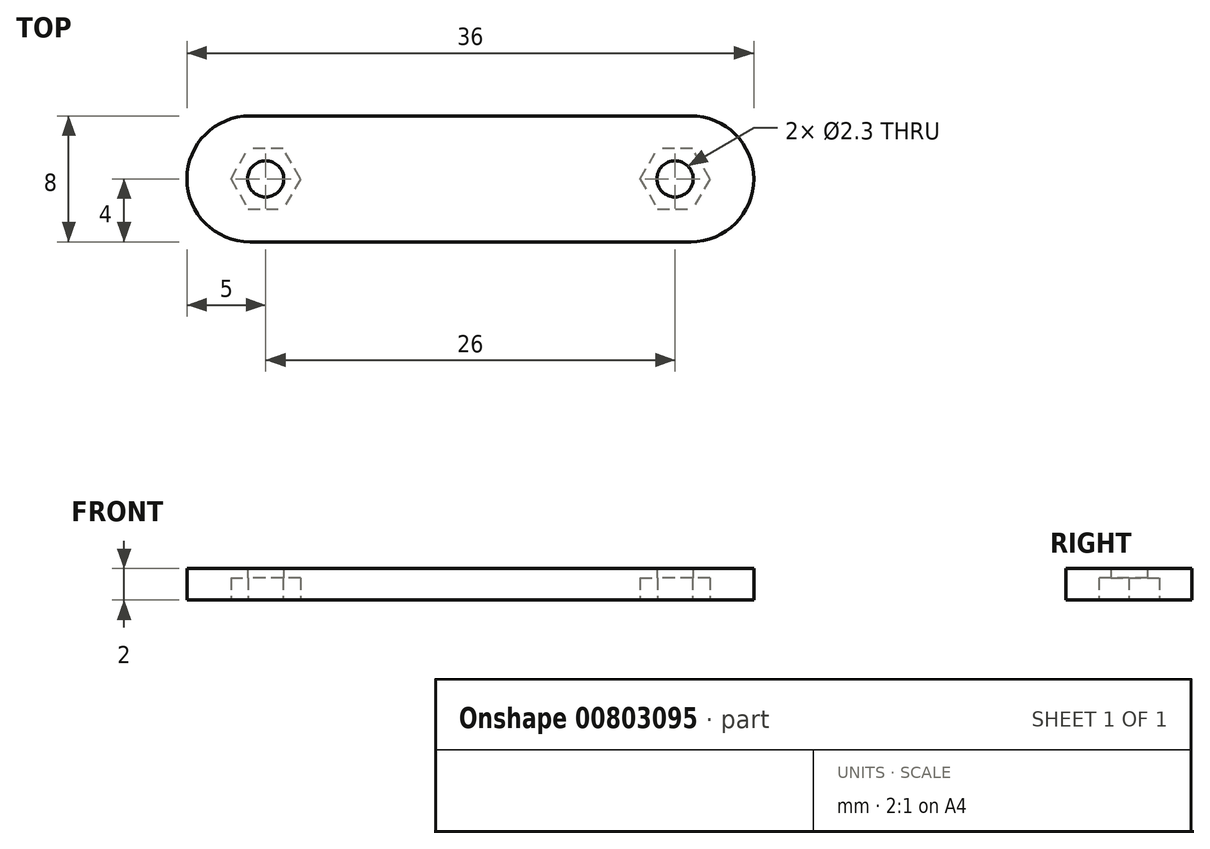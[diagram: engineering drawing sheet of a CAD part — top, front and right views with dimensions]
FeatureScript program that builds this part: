
annotation { "Feature Type Name" : "Feature", "Feature Type Description" : "" }
export const myFeature = defineFeature(function(context is Context, id is Id, definition is map)
    precondition{}
    {
        {
            var Q0;
            Q0=qCreatedBy(makeId("Top.planeOp"),FACE);
            var sketch = newSketch(context, id + "F0", { "sketchPlane" : qUnion([Q0])});
            skCircle(sketch, "E0", {"center": v(-13, 0) * mm, "radius": 1.15 * mm});
            skCircle(sketch, "E1.MirrorC", {"center": v(13, 0) * mm, "radius": 1.15 * mm});
            skSolve(sketch);
        }
        {
            var Q0;
            Q0=qCreatedBy(makeId("Top.planeOp"),FACE);
            var sketch = newSketch(context, id + "F1", { "sketchPlane" : qUnion([Q0])});
            skLineSegment(sketch, "E2.bottom", {"start": v(18, 4) * mm, "end": v(-18, 4) * mm});
            skLineSegment(sketch, "E2.top", {"start": v(18, -4) * mm, "end": v(-18, -4) * mm});
            skLineSegment(sketch, "E2.left", {"start": v(18, 4) * mm, "end": v(18, -4) * mm});
            skLineSegment(sketch, "E2.right", {"start": v(-18, 4) * mm, "end": v(-18, -4) * mm});
            skPoint(sketch, "E2.middle", {"position": v(0, 0) * mm});
            skSolve(sketch);
        }
        {
            var Q0;
            Q0=qCreatedBy(makeId("Top.planeOp"),FACE);
            var sketch = newSketch(context, id + "F2", { "sketchPlane" : qUnion([Q0])});
            skLineSegment(sketch, "E3", {"start": v(-13, 0) * mm, "end": v(-13, 4.8) * mm, "construction": true});
            skLineSegment(sketch, "E4", {"start": v(-13, 0) * mm, "end": v(-5.64, 0) * mm, "construction": true});
            skLineSegment(sketch, "E5", {"start": v(-13, 0) * mm, "end": v(-15.53, 4.38) * mm, "construction": true});
            skLineSegment(sketch, "E6", {"start": v(-10.79, 0) * mm, "end": v(-11.9, 1.91) * mm});
            skLineSegment(sketch, "E7", {"start": v(-11.9, 1.91) * mm, "end": v(-13, 1.91) * mm});
            skLineSegment(sketch, "E8.MirrorCS", {"start": v(-14.1, 1.91) * mm, "end": v(-13, 1.91) * mm});
            skLineSegment(sketch, "E9.MirrorCS", {"start": v(-15.21, 0) * mm, "end": v(-14.1, 1.91) * mm});
            skLineSegment(sketch, "E10.MirrorCS", {"start": v(-10.79, 0) * mm, "end": v(-11.9, -1.91) * mm});
            skLineSegment(sketch, "E11.MirrorCS", {"start": v(-11.9, -1.91) * mm, "end": v(-13, -1.91) * mm});
            skLineSegment(sketch, "E12.MirrorCS", {"start": v(-14.1, -1.91) * mm, "end": v(-13, -1.91) * mm});
            skLineSegment(sketch, "E13.MirrorCS", {"start": v(-15.21, 0) * mm, "end": v(-14.1, -1.91) * mm});
            skLineSegment(sketch, "E14.MirrorCS", {"start": v(15.21, 0) * mm, "end": v(14.1, -1.91) * mm});
            skLineSegment(sketch, "E15.MirrorCS", {"start": v(14.1, -1.91) * mm, "end": v(13, -1.91) * mm});
            skLineSegment(sketch, "E16.MirrorCS", {"start": v(14.1, 1.91) * mm, "end": v(13, 1.91) * mm});
            skLineSegment(sketch, "E17.MirrorCS", {"start": v(10.79, 0) * mm, "end": v(11.9, 1.91) * mm});
            skLineSegment(sketch, "E18.MirrorCS", {"start": v(15.21, 0) * mm, "end": v(14.1, 1.91) * mm});
            skLineSegment(sketch, "E19.MirrorCS", {"start": v(11.9, 1.91) * mm, "end": v(13, 1.91) * mm});
            skLineSegment(sketch, "E20.MirrorCS", {"start": v(11.9, -1.91) * mm, "end": v(13, -1.91) * mm});
            skLineSegment(sketch, "E21.MirrorCS", {"start": v(10.79, 0) * mm, "end": v(11.9, -1.91) * mm});
            skSolve(sketch);
        }
        {
            var Q0;
            Q0=qSketchRegion(id+"F1",true);
            extrude(context, id + "F3", {"entities" : qUnion([Q0]), "depth" : 2 * mm, "offsetDistance" : 25 * mm});
        }
        {
            var Q0;
            Q0=qSketchRegion(id+"F0",true);
            extrude(context, id + "F4", {"entities" : qUnion([Q0]), "operationType" : NewBodyOperationType.REMOVE, "endBound" : BoundingType.THROUGH_ALL, "depth" : 25 * mm, "offsetDistance" : 25 * mm});
        }
        {
            var Q0;
            Q0=qSketchRegion(id+"F2",true);
            extrude(context, id + "F5", {"entities" : qUnion([Q0]), "operationType" : NewBodyOperationType.REMOVE, "depth" : 1.4 * mm, "offsetDistance" : 25 * mm});
        }
        {
            var Q0;
            Q0=makeQuery(id+"F3.opExtrude","SWEPT_EDGE",EDGE,{"disambiguationData":[OSD([sQuery(id+"F1.wireOp",EDGE,"E2.bottom"),sQuery(id+"F1.wireOp",EDGE,"E2.right")])]});
            var Q1;
            Q1=makeQuery(id+"F3.opExtrude","SWEPT_EDGE",EDGE,{"disambiguationData":[OSD([sQuery(id+"F1.wireOp",EDGE,"E2.top"),sQuery(id+"F1.wireOp",EDGE,"E2.right")])]});
            var Q2;
            Q2=makeQuery(id+"F3.opExtrude","SWEPT_EDGE",EDGE,{"disambiguationData":[OSD([sQuery(id+"F1.wireOp",EDGE,"E2.top"),sQuery(id+"F1.wireOp",EDGE,"E2.left")])]});
            var Q3;
            Q3=makeQuery(id+"F3.opExtrude","SWEPT_EDGE",EDGE,{"disambiguationData":[OSD([sQuery(id+"F1.wireOp",EDGE,"E2.bottom"),sQuery(id+"F1.wireOp",EDGE,"E2.left")])]});
            fillet(context, id + "F6", {"entities" : qUnion([Q0, Q1, Q2, Q3]), "radius" : 4 * mm, "tangentPropagation" : true, "allowEdgeOverflow" : false});
        }
    });
